# Revit family: Lighting_Fixture-Wall-Astro-Digit
name_source: partatom
category: Lighting Fixtures
revit_build: Autodesk Revit 2014 (Build: 20130308_1515(x64)
units: mm (PartAtom-declared; Revit-internal decimal feet)

## types (3) — shared parameters
Apparent Load = 4 VA
Assembly Code = D5020200
Class = 2
Description = Recessed Wall Light
Dimmable = No
Energy Efficiency Rating = -
Head Rotation = 135.00°
Height = 80 mm  [stored 0.262467 ft]
IP Rating = IP20
Lamp = LED
Lamp included = Yes
Length = 64 mm  [stored 0.209974 ft]
Light Source Elevation = 1600 mm  [stored 5.24934 ft]
Light Source From Wall = 350 mm  [stored 1.14829 ft]
Luminaire Lamp Efficiency Rating = A
Manufacturer = Astro Lighting Ltd, CM20 2DP
Mountable on normally flammable surfaces = Yes
Number of Poles = 1
Product Documentation = http://www.astrolighting.co.uk
/kw/7164/7164_Digit
Rear Casing Material = Astro - ABS - Black
Suitable for bathroom zone = zone 3
Type Comments = Includes integral LED driver
Cut out size: 66mm high x 172mm wide
Requires 60mm recess minimum
Includes integral switch
URL = www.astrolighting.co.uk
Voltage = 230 V
Wattage Comments = 3W
Weight = 1.17 kg
Width = 190 mm

## per-type parameters (varying)
| type | Arm Angle | Casing Material | Model |
| 7164 Digit (Chrome) | 25.00° | Astro - Zinc - Chrome Finish | 7164 Digit Chrome |
| 7166 Digit (Bronze) | 20.00° | Astro - Zinc - Bronze | 7166 Digit Bronze |
| 7165 Digit (Matt Nickel) | 20.00° | Astro - Zinc - Matt Nickel | 7165 Digit Matt Nickel |

note: [stored X ft] marks values corroborated as IEEE doubles in the binary element streams (Revit-internal decimal feet)

## geometry (parser evidence)
native form markers: Sweep x3
no freeform markers — native parametric forms only
